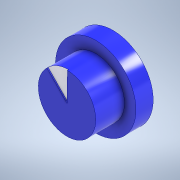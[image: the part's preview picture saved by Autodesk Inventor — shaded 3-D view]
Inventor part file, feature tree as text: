
AUTODESK INVENTOR PART (.ipt)
format: ipt  version: 2020 (Build 240168000, 168)  size: 124,928 bytes
history: native  units: mm
features: extrude x3, sketch x3
ambient origin geometry x8: Origin, YZ Plane, XZ Plane, XY Plane, X Axis, Y Axis, Z Axis, Center Point
bodies: Solid1 (feature_tree)
feature tree (6):
  extrude  "Extrusion1"  Depth=3.0mm TaperAngle=0.0deg
  extrude  "Extrusion2"  Depth=5.0mm TaperAngle=0.0deg
  extrude  "Extrusion3"  Depth=0.2mm TaperAngle=0.0deg
  sketch  "Sketch1"  dims[d0=14.0mm d1=3.0mm d2=0.0mm]
  sketch  "Sketch2"  dims[d3=10.0mm d4=5.0mm d5=0.0mm]
  sketch  "Sketch3"  dims[d6=45.0deg d7=0.2mm d8=0.0mm]
